# Revit family: 7.Обратный клапан для круглых каналов KOK
name_source: partatom
category: Оборудование
revit_build: Autodesk Revit 2016 (Build: 20151209_0715(x64)
units: mm (PartAtom-declared; Revit-internal decimal feet)

## family parameters
Всегда вертикально = Да
На основе рабочей плоскости = Нет
Общий = Нет
При загрузке вырезать с полостями = Нет
Размер круглого соединителя = Использовать диаметр
Тип детали = Нормальный
Точка расчета площади = Нет

## types (6) — shared parameters
Единица измерения = шт.
Завод изготовитель = KORF
Ключевая пометка = Вентиляция
Материал = Сталь серая
Наименование и тех.хар-ка = Обратный клапан для круглых каналов
Раздел = ОВ

## per-type parameters (varying)
| type | B | А | Б | Д | Д1 | Масса единицы | Тип, марка, обозначение | отступ |
| 100 | 35 мм | 80 мм | 27 мм | 100 мм | 98 мм | 0.2 кг | KOK 100 | 20 мм |
| 160 | 55 мм | 110 мм | 37 мм | 160 мм | 157 мм | 0.4 кг | KOK 160 | 40 мм |
| 200 | 70 мм | 140 мм | 52 мм | 200 мм | 196 мм | 0.6 кг | KOK 200 | 65 мм |
| 250 | 75 мм | 140 мм | 47 мм | 250 мм | 245 мм | 0.65 кг | KOK 250 | 65 мм |
| 315 | 75 мм | 140 мм | 47 мм | 315 мм | 309 мм | 0.8 кг | KOK 315 | 65 мм |
| 125 | 45 мм | 100 мм | 37 мм | 125 мм | 123 мм | 0,25 кг | KOK 125 | 40 мм |
